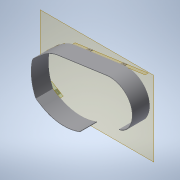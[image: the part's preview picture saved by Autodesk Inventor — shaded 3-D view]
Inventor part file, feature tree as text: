
AUTODESK INVENTOR PART (.ipt)
format: ipt  version: 2021 (Build 250183000, 183)  size: 204,800 bytes
history: native  units: in
note: dims shown in document units (in); Inventor stores cm internally (conversion verified against a paired STEP export)
features: reference x14, plane x4, extrude x4, sketch x4, other x2, fillet x1
ambient origin geometry x8: Origin, YZ Plane, XZ Plane, XY Plane, X Axis, Y Axis, Z Axis, Center Point
bodies: Solid1 (feature_tree)
feature tree (29):
  plane  "Work Plane1"
  extrude  "Extrusion1"  Depth=0.1024in
  fillet  "Fillet1"  Radius=1.0in
  plane  "Work Plane2"
  extrude  "Extrusion2"  Depth=0.75in
  plane  "Work Plane3"
  extrude  "Extrusion3"  Depth=0.75in
  plane  "Work Plane4"
  extrude  "Extrusion4"  Depth=0.1024in
  sketch  "Sketch1"  dims[d3=3.0in d4=0.0in d5=0.1024in d6=1.0in]
  reference  "Reference2"
  reference  "Reference3"
  reference  "Reference4"
  reference  "Reference5"
  reference  "Reference6"
  reference  "Reference7"
  reference  "Reference8"
  sketch  "Sketch2"  dims[d7=0.75in d8=2.65in]
  reference  "Reference9"
  reference  "Reference10"
  reference  "Reference11"
  sketch  "Sketch3"  dims[d9=5.35in d10=0.75in]
  reference  "Reference12"
  reference  "Reference13"
  sketch  "Sketch4"  dims[d11=0.1024in d12=0.0in d13=0.395in d14=0.395in d15=0.1024in d16=0.0in d19=0.395in d21=0.395in d22=0.1024in d23=0.0in]
  reference  "Reference14"
  reference  "Reference15"
  other  "Assembly1"
  other  "DiffMountRightipt:1"
